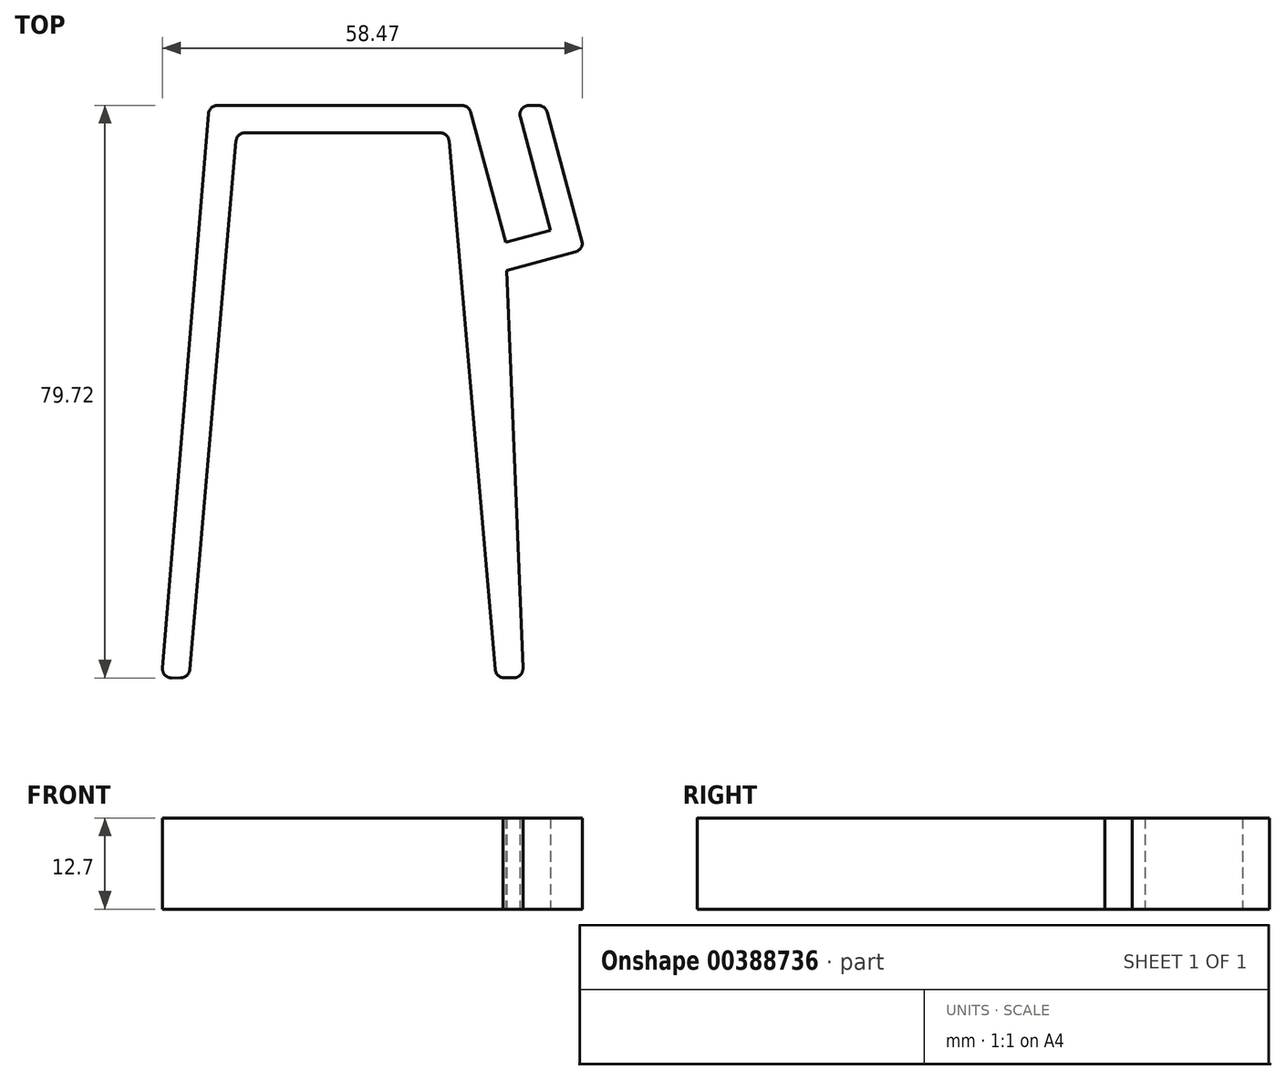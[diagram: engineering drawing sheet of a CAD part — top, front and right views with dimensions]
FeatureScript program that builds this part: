
annotation { "Feature Type Name" : "Feature", "Feature Type Description" : "" }
export const myFeature = defineFeature(function(context is Context, id is Id, definition is map)
    precondition{}
    {
        {
            var Q0;
            Q0=qCreatedBy(makeId("Top.planeOp"),FACE);
            var sketch = newSketch(context, id + "F0", { "sketchPlane" : qUnion([Q0])});
            skLineSegment(sketch, "E0", {"start": v(-13.17, 30.74) * mm, "end": v(13.97, 30.74) * mm});
            skLineSegment(sketch, "E1", {"start": v(-14.43, 29.58) * mm, "end": v(-20.87, -44.02) * mm});
            skLineSegment(sketch, "E2", {"start": v(15.23, 29.58) * mm, "end": v(21.67, -44.03) * mm});
            skPoint(sketch, "E3.visualSharp", {"position": v(-18.2, 34.53) * mm});
            skPoint(sketch, "E4.visualSharp", {"position": v(-24.78, -45.2) * mm});
            skLineSegment(sketch, "E5", {"start": v(17.04, 34.53) * mm, "end": v(-17.02, 34.53) * mm});
            skLineSegment(sketch, "E6", {"start": v(-18.29, 33.37) * mm, "end": v(-24.67, -43.82) * mm});
            skLineSegment(sketch, "E7", {"start": v(-23.4, -45.2) * mm, "end": v(-22.13, -45.18) * mm});
            skPoint(sketch, "E8.visualSharp", {"position": v(21.77, -45.17) * mm});
            skArc(sketch, "E8.filletArc", {"start": v(21.67, -44.03) * mm, "mid": v(22.01, -44.79) * mm, "end": v(22.75, -45.17) * mm});
            skPoint(sketch, "E9.visualSharp", {"position": v(15.13, 30.74) * mm});
            skArc(sketch, "E9.filletArc", {"start": v(15.23, 29.58) * mm, "mid": v(14.83, 30.4) * mm, "end": v(13.97, 30.74) * mm});
            skPoint(sketch, "E10.visualSharp", {"position": v(-14.33, 30.74) * mm});
            skArc(sketch, "E10.filletArc", {"start": v(-13.17, 30.74) * mm, "mid": v(-14.03, 30.4) * mm, "end": v(-14.43, 29.58) * mm});
            skPoint(sketch, "E11.visualSharp", {"position": v(-20.97, -45.17) * mm});
            skArc(sketch, "E11.filletArc", {"start": v(-22.13, -45.18) * mm, "mid": v(-21.28, -44.85) * mm, "end": v(-20.87, -44.02) * mm});
            skArc(sketch, "E12.filletArc", {"start": v(-24.67, -43.82) * mm, "mid": v(-24.33, -44.79) * mm, "end": v(-23.4, -45.2) * mm});
            skArc(sketch, "E13.filletArc", {"start": v(-17.02, 34.53) * mm, "mid": v(-17.88, 34.2) * mm, "end": v(-18.29, 33.37) * mm});
            skLineSegment(sketch, "E14", {"start": v(23.12, 15.48) * mm, "end": v(18.26, 33.6) * mm});
            skLineSegment(sketch, "E15", {"start": v(23.12, 15.48) * mm, "end": v(29.37, 17.16) * mm});
            skLineSegment(sketch, "E16", {"start": v(22.75, -45.17) * mm, "end": v(24.26, -45.17) * mm});
            skLineSegment(sketch, "E17", {"start": v(26.37, 34.53) * mm, "end": v(27.69, 34.53) * mm});
            skLineSegment(sketch, "E18", {"start": v(29.37, 17.16) * mm, "end": v(25.14, 32.93) * mm});
            skPoint(sketch, "E19", {"position": v(24.72, 34.53) * mm});
            skLineSegment(sketch, "E20", {"start": v(25.53, -43.85) * mm, "end": v(23.27, 11.57) * mm});
            skLineSegment(sketch, "E21", {"start": v(30.97, 13.63) * mm, "end": v(23.27, 11.57) * mm});
            skLineSegment(sketch, "E22", {"start": v(23.27, 11.57) * mm, "end": v(30.97, 13.63) * mm});
            skLineSegment(sketch, "E23", {"start": v(30.97, 13.63) * mm, "end": v(32.86, 14.14) * mm});
            skPoint(sketch, "E24.visualSharp", {"position": v(25.58, -45.17) * mm});
            skArc(sketch, "E24.filletArc", {"start": v(24.26, -45.17) * mm, "mid": v(25.18, -44.78) * mm, "end": v(25.53, -43.85) * mm});
            skPoint(sketch, "E25.visualSharp", {"position": v(33.8, 14.4) * mm});
            skArc(sketch, "E25.filletArc", {"start": v(32.86, 14.14) * mm, "mid": v(33.53, 14.6) * mm, "end": v(33.8, 15.37) * mm});
            skPoint(sketch, "E26.visualSharp", {"position": v(18.01, 34.53) * mm});
            skArc(sketch, "E26.filletArc", {"start": v(18.26, 33.6) * mm, "mid": v(17.8, 34.27) * mm, "end": v(17.04, 34.53) * mm});
            skArc(sketch, "E27.filletArc", {"start": v(26.37, 34.53) * mm, "mid": v(25.36, 34.03) * mm, "end": v(25.14, 32.93) * mm});
            skLineSegment(sketch, "E28", {"start": v(33.8, 15.37) * mm, "end": v(28.91, 33.6) * mm});
            skPoint(sketch, "E29.visualSharp", {"position": v(28.66, 34.53) * mm});
            skArc(sketch, "E29.filletArc", {"start": v(28.91, 33.6) * mm, "mid": v(28.46, 34.27) * mm, "end": v(27.69, 34.53) * mm});
            skSolve(sketch);
        }
        {
            var Q0;
            Q0=makeQuery(id+"F0.imprint","IMPRINT",FACE,{"disambiguationData":[TD([[makeQuery(id+"F0.imprint","IMPRINT",EDGE,{"derivedFrom":sQuery(id+"F0.wireOp",EDGE,"E0")}),1.0]])]});
            extrude(context, id + "F1", {"entities" : qUnion([Q0]), "depth" : 12.7 * mm});
        }
    });
